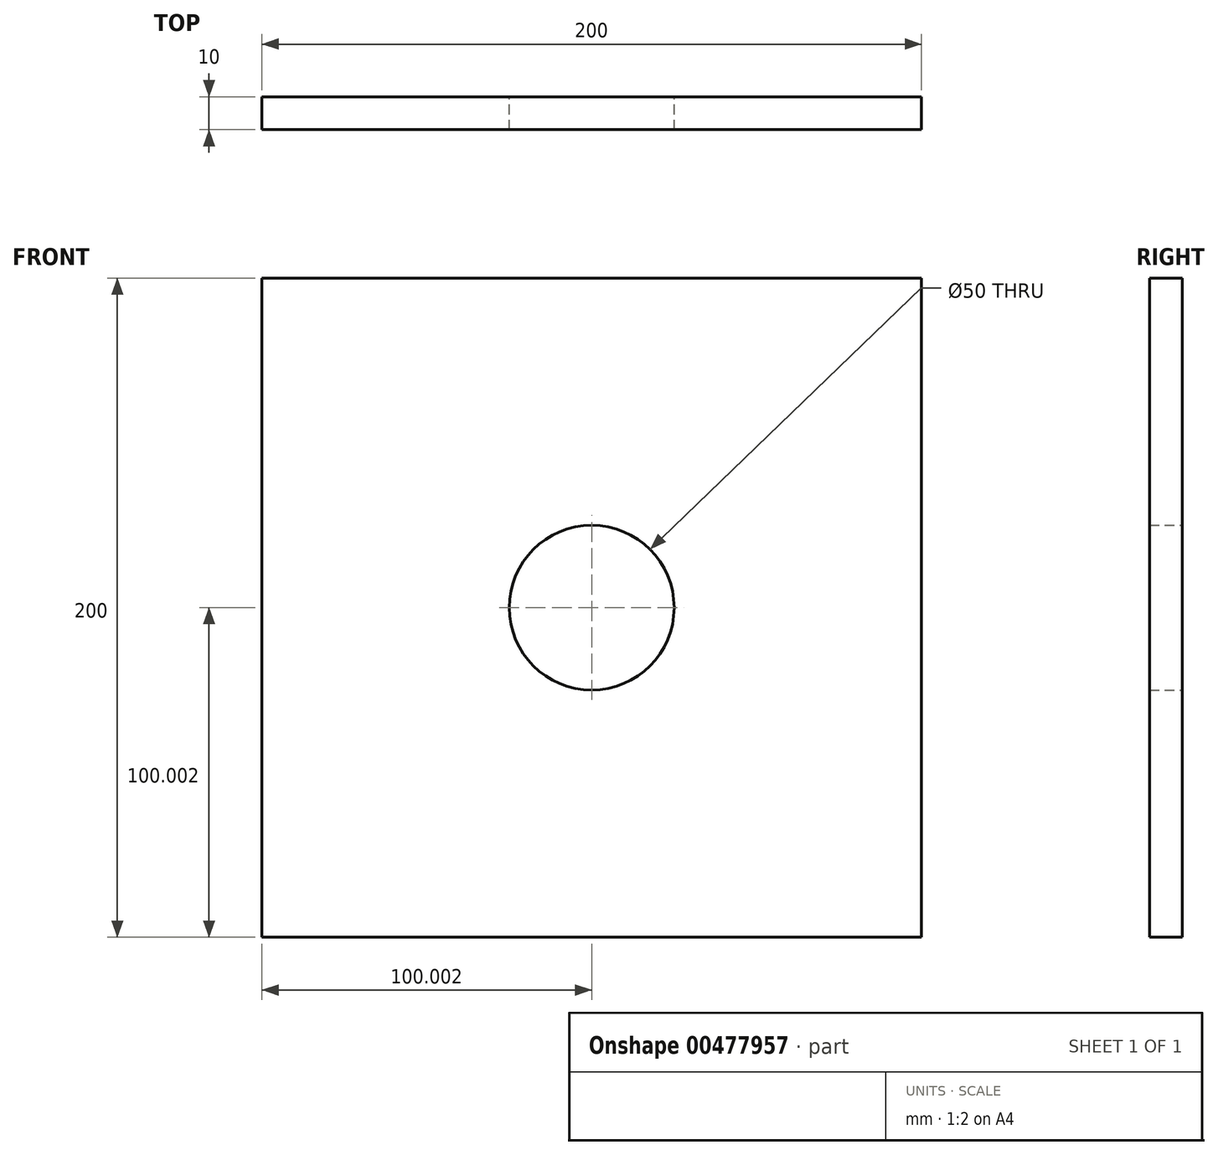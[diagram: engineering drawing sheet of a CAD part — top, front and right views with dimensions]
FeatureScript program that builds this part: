
annotation { "Feature Type Name" : "Feature", "Feature Type Description" : "" }
export const myFeature = defineFeature(function(context is Context, id is Id, definition is map)
    precondition{}
    {
        {
            var Q0;
            Q0=qCreatedBy(makeId("Front.planeOp"),FACE);
            var sketch = newSketch(context, id + "F0", { "sketchPlane" : qUnion([Q0])});
            skLineSegment(sketch, "E0.bottom", {"start": v(-147.1, 144.15) * mm, "end": v(52.9, 144.15) * mm});
            skLineSegment(sketch, "E0.top", {"start": v(-147.1, -55.85) * mm, "end": v(52.9, -55.85) * mm});
            skLineSegment(sketch, "E0.left", {"start": v(-147.1, 144.15) * mm, "end": v(-147.1, -55.85) * mm});
            skLineSegment(sketch, "E0.right", {"start": v(52.9, 144.15) * mm, "end": v(52.9, -55.85) * mm});
            skCircle(sketch, "E1", {"center": v(-47.1, 44.15) * mm, "radius": 25 * mm});
            skPoint(sketch, "E1.centerSnap0", {"position": v(-147.1, 44.15) * mm});
            skPoint(sketch, "E1.centerSnap1", {"position": v(-47.1, 144.15) * mm});
            skSolve(sketch);
        }
        {
            var Q0;
            Q0=makeQuery(id+"F0.imprint","IMPRINT",FACE,{"disambiguationData":[TD([[makeQuery(id+"F0.imprint","IMPRINT",EDGE,{"derivedFrom":sQuery(id+"F0.wireOp",EDGE,"E0.bottom")}),-1.0]])]});
            extrude(context, id + "F1", {"entities" : qUnion([Q0]), "depth" : 10 * mm, "offsetDistance" : 25 * mm});
        }
    });
